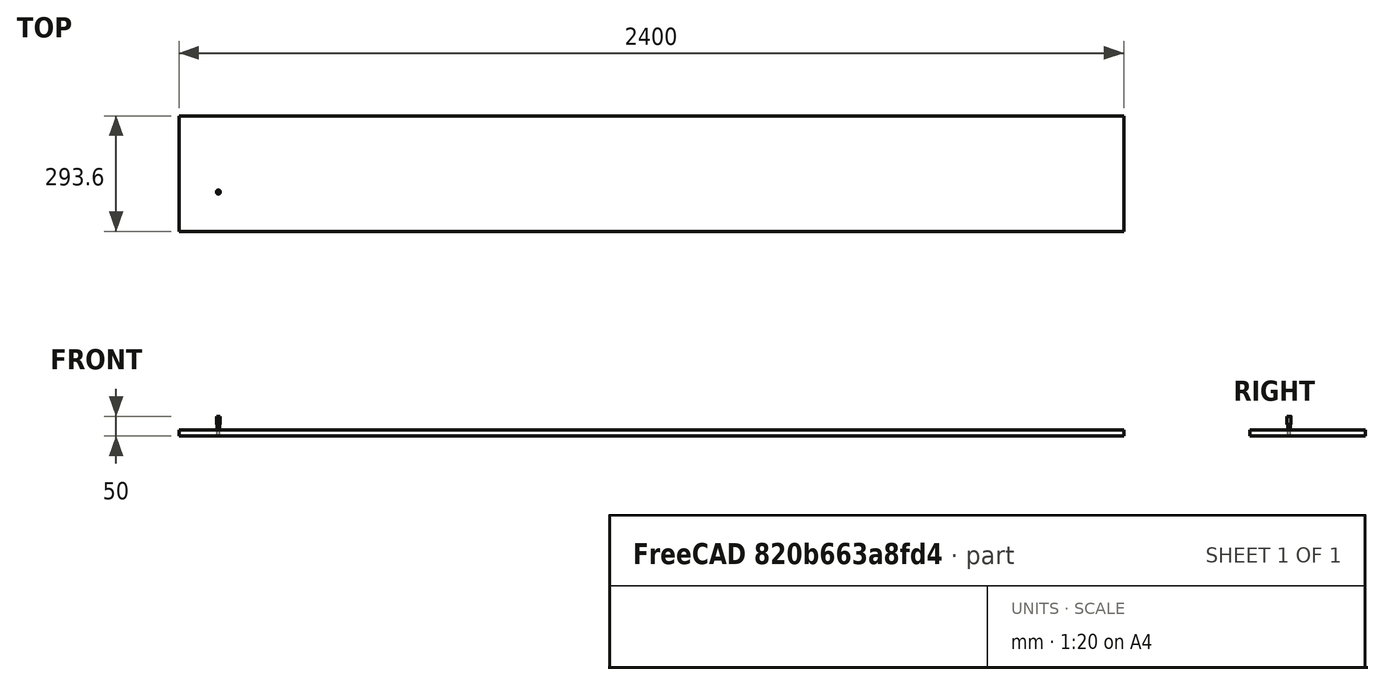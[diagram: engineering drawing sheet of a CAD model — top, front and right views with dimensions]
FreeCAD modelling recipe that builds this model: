
FCSTD DOCUMENT  (FreeCAD 0.19R14555 (Git shallow))
Label: Shelves
License: All rights reserved
LicenseURL: http://en.wikipedia.org/wiki/All_rights_reserved
objects: Part::FeaturePython×3, Path::FeaturePython×3, App::DocumentObjectGroup×2, Sketcher::SketchObject×1, PartDesign::Pad×1, PartDesign::Fillet×1, PartDesign::Body×1, App::FeaturePython×1, Path::FeatureCompoundPython×1, Mesh::FeaturePython×1
note: 10 computed .brp shape members not serialized (recipe doc carries the construction recipe); baked Part::Feature solids carry a one-line shape summary decoded from their .brp

FEATURE [Sketcher::SketchObject] Sketch
  FullyConstrained = true
  MapMode = 5
  Support = -> [XY_Plane]
  sketch-geometry (4):
    g0: LineSegment StartX=-100 StartY=-100 StartZ=0 EndX=2300 EndY=-100 EndZ=0
    g1: LineSegment StartX=2300 StartY=-100 StartZ=0 EndX=2300 EndY=193.6 EndZ=0
    g2: LineSegment StartX=2300 StartY=193.6 StartZ=0 EndX=-100 EndY=193.6 EndZ=0
    g3: LineSegment StartX=-100 StartY=193.6 StartZ=0 EndX=-100 EndY=-100 EndZ=0
  constraints (12):
    c: Coincident(g0,g1)
    c: Coincident(g1,g2)
    c: Coincident(g2,g3)
    c: Coincident(g3,g0)
    c: Horizontal(g0)
    c: Horizontal(g2)
    c: Vertical(g1)
    c: Vertical(g3)
    c: DistanceX(g0,g-1) = 100
    c: DistanceY(g0,g-1) = 100
    c: DistanceX(g0,g0) = 2400
    c: DistanceY(g3,g3) = 293.6
FEATURE [PartDesign::Pad] Pad
  Direction = (1,1,1)
  Length = 16
  Length2 = 100
  Profile = -> Sketch
  Type = 0
FEATURE [PartDesign::Fillet] Fillet
  Base = -> Pad [Edge8,Edge5]
  BaseFeature = -> Pad
  Radius = 10
  SupportTransform = false
FEATURE [PartDesign::Body] Body
  Group = -> [Sketch,Pad,Fillet]
  Origin = -> Origin
  Tip = -> Fillet
FEATURE [App::FeaturePython] SetupSheet  # Path/CAM operation (typed FeaturePython)
  ClearanceHeightExpression = OpStockZMax+SetupSheet.ClearanceHeightOffset
  ClearanceHeightOffset = 5
  CoolantMode = 0
  CoolantModes = None | Flood | Mist
  FinalDepthExpression = OpFinalDepth
  HorizRapid = 0
  SafeHeightExpression = OpStockZMax+SetupSheet.SafeHeightOffset
  SafeHeightOffset = 3
  StartDepthExpression = OpStartDepth
  StepDownExpression = OpToolDiameter
  VertRapid = 0
FEATURE [Part::FeaturePython] Clone  label="Model-Body"  # Draft clone (typed FeaturePython)
  AttacherType = Attacher::AttachEngine3D
  Fuse = false
  Objects = -> [Body]
  PathResource = Model
  Scale = (1,1,1)
FEATURE [App::DocumentObjectGroup] Model
  Group = -> [Clone]
FEATURE [Part::FeaturePython] Stock001  # WARN: FeaturePython — macro-defined, semantics opaque (R4)
  Height = 16
  Length = 2400
  Placement = pos=(-100,-100,0) rot=(0,0,1;0rad)
  StockType = CreateBox
  Width = 293.6
FEATURE [Part::FeaturePython] ToolBit001  label="6.4mm Endmill"  # Path/CAM toolbit (typed FeaturePython)
  BitPropertyNames = Chipload | CuttingEdgeHeight | Diameter | Flutes | Length | Material | ShankDiameter
  BitShape = /app/freecad/Mod/Path/Tools/Shape/endmill.fcstd
  Chipload = 0
  CuttingEdgeHeight = 30
  Diameter = 6.4
  File = <userpath>/Documents/MensShed/FreeCAD/Bit/6.4mm_Endmill.fctb
  Flutes = 0
  Length = 50
  Material = 0
  ShankDiameter = 10
  ShapeName = endmill
FEATURE [Path::FeaturePython] __4mm_Endmill  label="6.4mm Endmill001"  # Path/CAM operation (typed FeaturePython)
  HorizFeed = 60
  HorizRapid = 0
  SpindleDir = 0
  SpindleSpeed = 10000
  Tool = -> ToolBit001
  ToolNumber = 1
  VertFeed = 60
  VertRapid = 0
  expr: HorizRapid = SetupSheet.HorizRapid
  expr: VertRapid = SetupSheet.VertRapid
FEATURE [App::DocumentObjectGroup] Tools
  Group = -> [__4mm_Endmill]
FEATURE [Path::FeaturePython] Profile  # Path/CAM operation (typed FeaturePython)
  Active = true
  AreaParams:
    Tolerance = 1e-07
    FitArcs = True
    Simplify = False
    CleanDistance = 0.0
    Accuracy = 0.01
    Unit = 1.0
    MinArcPoints = 4
    MaxArcPoints = 100
    ClipperScale = 10000000.0
    Fill = 0
    Coplanar = 0
    Reorient = True
    Outline = False
    Explode = False
    OpenMode = 0
    Deflection = 0.01
    SubjectFill = 0
    ClipFill = 0
    Offset = -3.2
    ExtraPass = 0
    Stepover = 0.0
    LastStepover = 0.0
    JoinType = 0
    EndType = 0
    MiterLimit = 2.0
    RoundPrecision = 0.0
    PocketMode = 0
    ToolRadius = 1.0
    PocketExtraOffset = 0.0
    PocketStepover = 0.0
    PocketLastStepover = 0.0
    FromCenter = False
    Angle = 45.0
    AngleShift = 0.0
    Shift = 0.0
    Thicken = False
    SectionCount = -1
    Stepdown = 1.0
    SectionOffset = 0.0
    SectionTolerance = 1e-06
    SectionMode = 2
    Project = False
  AttemptInverseAngle = true
  Base = -> [Clone]
  ClearanceHeight = 21
  CoolantMode = None
  CycleTime = 00:05:06
  Direction = 0
  EnableRotation = 0
  FinalDepth = 0
  HandleMultipleFeatures = 0
  InverseAngle = false
  JoinType = 0
  LimitDepthToFace = true
  MiterLimit = 0.1
  OffsetExtra = 0
  OpFinalDepth = 16
  OpStartDepth = 22.4
  OpStockZMax = 16
  OpStockZMin = 0
  OpToolDiameter = 6.4
  PathParams = {'orientation': 1, 'feedrate': 60.0, 'feedrate_v': 60.0, 'verbose': True, 'resume_height': 19.0, 'retraction': 21.0, 'return_end': True, 'preamble': False}
  ReverseDirection = false
  SafeHeight = 19
  Side = 1
  StartDepth = 16
  StartPoint = (0,0,0)
  StepDown = 6.4
  ToolController = -> __4mm_Endmill
  UseComp = true
  UseStartPoint = false
  processCircles = false
  processHoles = false
  processPerimeter = true
  expr: ClearanceHeight = OpStockZMax + SetupSheet.ClearanceHeightOffset
  expr: SafeHeight = OpStockZMax + SetupSheet.SafeHeightOffset
  expr: StepDown = OpToolDiameter
  expr: FinalDepth = 0
  expr: StartDepth = 16
FEATURE [Path::FeatureCompoundPython] Operations  # Path/CAM operation (typed FeaturePython)
  Group = -> [Profile]
  UsePlacements = false
FEATURE [Path::FeaturePython] Job  # Path/CAM operation (typed FeaturePython)
  CycleTime = 00:05:06
  Fixtures = G54
  GeometryTolerance = 0.01
  LastPostProcessDate = 2021-12-26 15:32:35.348718
  LastPostProcessOutput = <userpath>/Documents/MensShed/Shelves.ngc
  Model = -> Model
  Operations = -> Operations
  OrderOutputBy = 0
  PostProcessor = 7
  PostProcessorOutputFile = <userpath>/Documents/MensShed/Shelves.ngc
  SetupSheet = -> SetupSheet
  SplitOutput = false
  Stock = -> Stock001
  Tools = -> Tools
FEATURE [Mesh::FeaturePython] CutMaterial  # WARN: FeaturePython — macro-defined, semantics opaque (R4)
